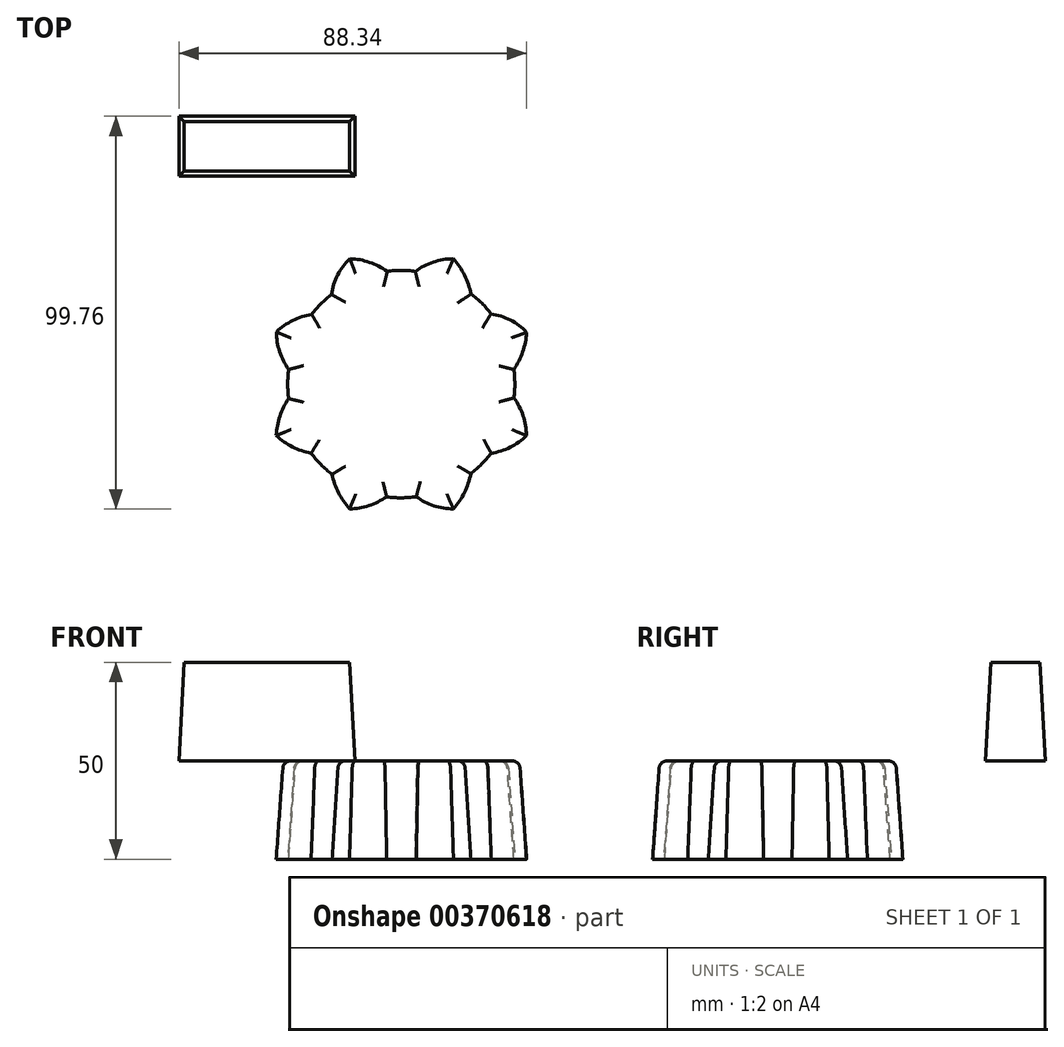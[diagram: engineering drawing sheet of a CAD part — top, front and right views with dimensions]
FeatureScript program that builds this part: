
annotation { "Feature Type Name" : "Feature", "Feature Type Description" : "" }
export const myFeature = defineFeature(function(context is Context, id is Id, definition is map)
    precondition{}
    {
        {
            var Q0;
            Q0=qCreatedBy(makeId("Top.planeOp"),FACE);
            var sketch = newSketch(context, id + "F0", { "sketchPlane" : qUnion([Q0])});
            skArc(sketch, "E0", {"start": v(-15.98, -20.72) * mm, "mid": v(-14.73, -24.95) * mm, "end": v(-12.42, -28.7) * mm});
            skArc(sketch, "E1", {"start": v(-21.94, -14.76) * mm, "mid": v(-19.2, -17.99) * mm, "end": v(-15.98, -20.72) * mm});
            skArc(sketch, "E2", {"start": v(-29.98, -11.13) * mm, "mid": v(-26.21, -13.5) * mm, "end": v(-21.94, -14.76) * mm});
            skArc(sketch, "E3", {"start": v(-26.82, -2.91) * mm, "mid": v(-28.95, -6.81) * mm, "end": v(-29.98, -11.13) * mm});
            skArc(sketch, "E4", {"start": v(-12.42, -28.7) * mm, "mid": v(-8.08, -27.74) * mm, "end": v(-4.19, -25.6) * mm});
            skArc(sketch, "E5", {"start": v(-4.19, -25.6) * mm, "mid": v(0.04, -25.92) * mm, "end": v(4.26, -25.58) * mm});
            skArc(sketch, "E6", {"start": v(-4.19, -25.6) * mm, "mid": v(0.04, -25.93) * mm, "end": v(4.26, -25.58) * mm});
            skArc(sketch, "E7", {"start": v(4.26, -25.58) * mm, "mid": v(8.1, -27.78) * mm, "end": v(12.43, -28.71) * mm});
            skArc(sketch, "E8", {"start": v(12.43, -28.71) * mm, "mid": v(14.76, -24.9) * mm, "end": v(16.06, -20.63) * mm});
            skArc(sketch, "E9", {"start": v(16.06, -20.63) * mm, "mid": v(19.16, -17.83) * mm, "end": v(21.92, -14.72) * mm});
            skArc(sketch, "E10", {"start": v(21.92, -14.72) * mm, "mid": v(26.24, -13.56) * mm, "end": v(30, -11.15) * mm});
            skArc(sketch, "E11", {"start": v(30, -11.15) * mm, "mid": v(29.03, -6.72) * mm, "end": v(26.79, -2.77) * mm});
            skArc(sketch, "E12", {"start": v(26.79, -2.77) * mm, "mid": v(27.07, 1.3) * mm, "end": v(26.75, 5.37) * mm});
            skArc(sketch, "E13", {"start": v(26.75, 5.37) * mm, "mid": v(28.94, 9.32) * mm, "end": v(30.02, 13.7) * mm});
            skArc(sketch, "E14", {"start": v(30.02, 13.7) * mm, "mid": v(26.2, 16.28) * mm, "end": v(21.72, 17.35) * mm});
            skArc(sketch, "E15", {"start": v(21.72, 17.35) * mm, "mid": v(19.23, 20.53) * mm, "end": v(16.04, 23) * mm});
            skArc(sketch, "E16", {"start": v(16.04, 23) * mm, "mid": v(14.83, 27.4) * mm, "end": v(12.45, 31.28) * mm});
            skArc(sketch, "E17", {"start": v(12.45, 31.28) * mm, "mid": v(7.96, 30.28) * mm, "end": v(3.99, 27.98) * mm});
            skArc(sketch, "E18", {"start": v(3.99, 27.98) * mm, "mid": v(-0.01, 28.37) * mm, "end": v(-4.02, 27.99) * mm});
            skArc(sketch, "E19", {"start": v(-4.02, 27.99) * mm, "mid": v(-7.97, 30.25) * mm, "end": v(-12.4, 31.29) * mm});
            skArc(sketch, "E20", {"start": v(-12.4, 31.29) * mm, "mid": v(-14.96, 27.48) * mm, "end": v(-16.05, 23.03) * mm});
            skArc(sketch, "E21", {"start": v(-16.05, 23.03) * mm, "mid": v(-19.17, 20.4) * mm, "end": v(-21.8, 17.3) * mm});
            skArc(sketch, "E22", {"start": v(-21.8, 17.3) * mm, "mid": v(-26.16, 16.12) * mm, "end": v(-29.98, 13.72) * mm});
            skArc(sketch, "E23", {"start": v(-29.98, 13.72) * mm, "mid": v(-29.02, 9.32) * mm, "end": v(-26.8, 5.4) * mm});
            skArc(sketch, "E24", {"start": v(-26.8, 5.4) * mm, "mid": v(-27.13, 1.24) * mm, "end": v(-26.82, -2.91) * mm});
            skSolve(sketch);
        }
        {
            var Q0;
            Q0 = qSketchRegion(id + "F0", true);
            extrude(context, id + "F1", {"entities" : qUnion([Q0]), "oppositeDirection" : true, "depth" : 25 * mm, "hasDraft" : true, "draftAngle" : 4 * degree});
        }
        {
            var Q0;
            Q0=makeQuery(id+"F1.opExtrude","CAP_FACE",FACE,{"disambiguationData":[OSD([sQuery(id+"F0.wireOp",EDGE,"E0"),sQuery(id+"F0.wireOp",EDGE,"E1"),sQuery(id+"F0.wireOp",EDGE,"E2"),sQuery(id+"F0.wireOp",EDGE,"E3"),sQuery(id+"F0.wireOp",EDGE,"E4"),sQuery(id+"F0.wireOp",EDGE,"E6"),sQuery(id+"F0.wireOp",EDGE,"E7"),sQuery(id+"F0.wireOp",EDGE,"E8"),sQuery(id+"F0.wireOp",EDGE,"E9"),sQuery(id+"F0.wireOp",EDGE,"E10"),sQuery(id+"F0.wireOp",EDGE,"E11"),sQuery(id+"F0.wireOp",EDGE,"E12"),sQuery(id+"F0.wireOp",EDGE,"E13"),sQuery(id+"F0.wireOp",EDGE,"E14"),sQuery(id+"F0.wireOp",EDGE,"E15"),sQuery(id+"F0.wireOp",EDGE,"E16"),sQuery(id+"F0.wireOp",EDGE,"E17"),sQuery(id+"F0.wireOp",EDGE,"E18"),sQuery(id+"F0.wireOp",EDGE,"E19"),sQuery(id+"F0.wireOp",EDGE,"E20"),sQuery(id+"F0.wireOp",EDGE,"E21"),sQuery(id+"F0.wireOp",EDGE,"E22"),sQuery(id+"F0.wireOp",EDGE,"E23"),sQuery(id+"F0.wireOp",EDGE,"E24")])],"isStart":true});
            fillet(context, id + "F2", {"entities" : qUnion([Q0]), "radius" : 2 * mm, "tangentPropagation" : true, "allowEdgeOverflow" : false});
        }
        {
            var Q0;
            Q0=qCreatedBy(makeId("Top.planeOp"),FACE);
            var sketch = newSketch(context, id + "F3", { "sketchPlane" : qUnion([Q0])});
            skLineSegment(sketch, "E25.bottom", {"start": v(-56.5, 69.26) * mm, "end": v(-11.8, 69.26) * mm});
            skLineSegment(sketch, "E25.top", {"start": v(-56.5, 54.08) * mm, "end": v(-11.8, 54.08) * mm});
            skLineSegment(sketch, "E25.left", {"start": v(-56.5, 69.26) * mm, "end": v(-56.5, 54.08) * mm});
            skLineSegment(sketch, "E25.right", {"start": v(-11.8, 69.26) * mm, "end": v(-11.8, 54.08) * mm});
            skSolve(sketch);
        }
        {
            var Q0;
            Q0=makeQuery(id+"F3.imprint","IMPRINT",FACE,{"disambiguationData":[TD([[makeQuery(id+"F3.imprint","IMPRINT",EDGE,{"derivedFrom":sQuery(id+"F3.wireOp",EDGE,"E25.bottom")}),-1.0]])]});
            extrude(context, id + "F4", {"entities" : qUnion([Q0]), "depth" : 25 * mm, "hasDraft" : true, "draftAngle" : 3 * degree, "draftPullDirection" : true});
        }
    });
